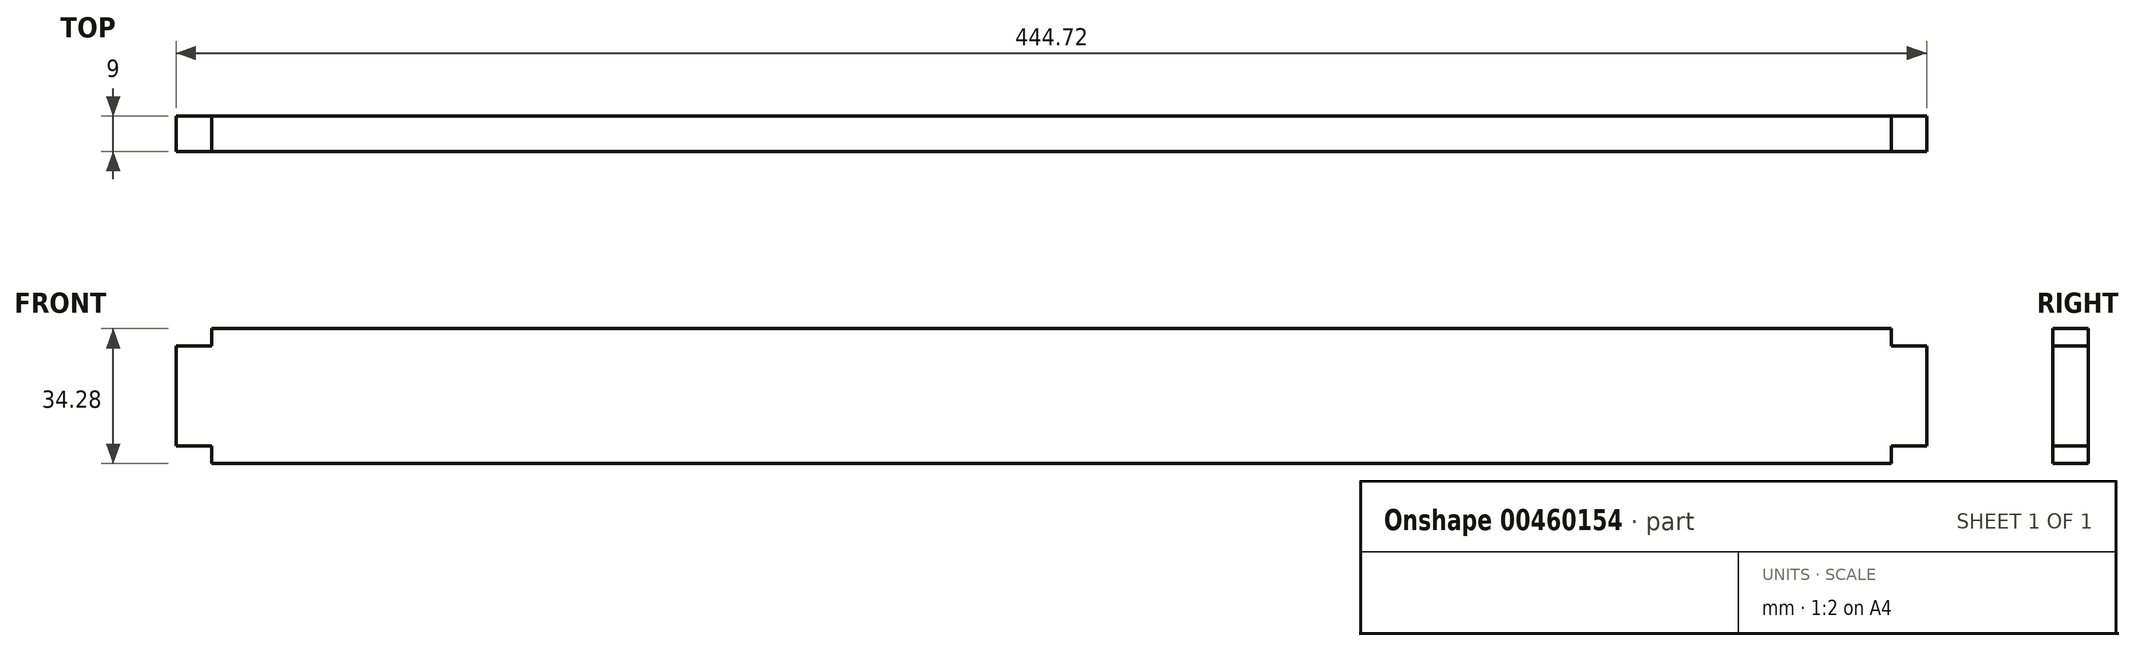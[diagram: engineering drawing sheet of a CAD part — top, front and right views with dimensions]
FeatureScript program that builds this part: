
annotation { "Feature Type Name" : "Feature", "Feature Type Description" : "" }
export const myFeature = defineFeature(function(context is Context, id is Id, definition is map)
    precondition{}
    {
        {
            var Q0;
            Q0=qCreatedBy(makeId("Front.planeOp"),FACE);
            var sketch = newSketch(context, id + "F0", { "sketchPlane" : qUnion([Q0])});
            skLineSegment(sketch, "E0.bottom", {"start": v(213.36, -17.15) * mm, "end": v(-213.36, -17.15) * mm});
            skLineSegment(sketch, "E0.top", {"start": v(213.36, 17.15) * mm, "end": v(-213.36, 17.15) * mm});
            skLineSegment(sketch, "E0.left", {"start": v(213.36, -17.15) * mm, "end": v(213.36, 17.15) * mm});
            skLineSegment(sketch, "E0.right", {"start": v(-213.36, -17.15) * mm, "end": v(-213.36, 17.15) * mm});
            skPoint(sketch, "E0.middle", {"position": v(0, 0) * mm});
            skLineSegment(sketch, "E1.bottom", {"start": v(222.36, -12.7) * mm, "end": v(213.36, -12.7) * mm});
            skLineSegment(sketch, "E1.top", {"start": v(222.36, 12.7) * mm, "end": v(213.36, 12.7) * mm});
            skLineSegment(sketch, "E1.left", {"start": v(222.36, -12.7) * mm, "end": v(222.36, 12.7) * mm});
            skLineSegment(sketch, "E1.right", {"start": v(213.36, -12.7) * mm, "end": v(213.36, 12.7) * mm});
            skPoint(sketch, "E1.middle", {"position": v(217.86, 0) * mm});
            skLineSegment(sketch, "E2.bottom", {"start": v(-213.36, -12.7) * mm, "end": v(-222.36, -12.7) * mm});
            skLineSegment(sketch, "E2.top", {"start": v(-213.36, 12.7) * mm, "end": v(-222.36, 12.7) * mm});
            skLineSegment(sketch, "E2.left", {"start": v(-213.36, -12.7) * mm, "end": v(-213.36, 12.7) * mm});
            skLineSegment(sketch, "E2.right", {"start": v(-222.36, -12.7) * mm, "end": v(-222.36, 12.7) * mm});
            skPoint(sketch, "E2.middle", {"position": v(-217.86, 0) * mm});
            skLineSegment(sketch, "E3.bottom", {"start": v(179.96, 17.15) * mm, "end": v(-179.96, 17.15) * mm, "construction": true});
            skLineSegment(sketch, "E3.top", {"start": v(179.96, -17.14) * mm, "end": v(-179.96, -17.14) * mm, "construction": true});
            skLineSegment(sketch, "E3.left", {"start": v(179.96, 17.15) * mm, "end": v(179.96, -17.15) * mm, "construction": true});
            skLineSegment(sketch, "E3.right", {"start": v(-179.96, 17.15) * mm, "end": v(-179.96, -17.14) * mm, "construction": true});
            skSolve(sketch);
        }
        {
            var Q0;
            {var subQ3=sQuery(id+"F0.wireOp",EDGE,"E0.bottom");Q0=makeQuery(id+"F0.imprint","IMPRINT",FACE,{"disambiguationData":[TD([[makeQuery(id+"F0.imprint","IMPRINT",EDGE,{"derivedFrom":subQ3}),-1.0]])]});}
            var Q1;
            Q1=makeQuery(id+"F0.imprint","IMPRINT",FACE,{"disambiguationData":[TD([[makeQuery(id+"F0.imprint","IMPRINT",EDGE,{"derivedFrom":sQuery(id+"F0.wireOp",EDGE,"E2.bottom")}),-1.0]])]});
            var Q2;
            Q2=makeQuery(id+"F0.imprint","IMPRINT",FACE,{"disambiguationData":[TD([[makeQuery(id+"F0.imprint","IMPRINT",EDGE,{"derivedFrom":sQuery(id+"F0.wireOp",EDGE,"E1.bottom")}),-1.0]])]});
            extrude(context, id + "F1", {"entities" : qUnion([Q0, Q1, Q2]), "endBound" : BoundingType.SYMMETRIC, "depth" : 9 * mm});
        }
    });
